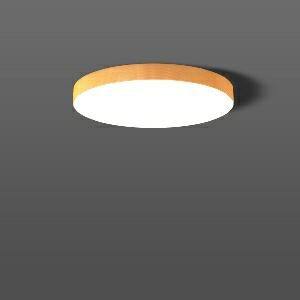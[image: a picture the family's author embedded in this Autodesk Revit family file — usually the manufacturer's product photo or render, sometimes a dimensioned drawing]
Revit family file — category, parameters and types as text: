
# Revit family: flatliner_slim_312283_002_1_33f7
name_source: partatom
category: Lighting Fixtures
units: mm (PartAtom-declared; Revit-internal decimal feet)

## family parameters
Cut with Voids When Loaded = No
Host = Face
Light Source = No
Part Type = Normal
Room Calculation Point = No
Round Connector Dimension = Use Diameter
Shared = No

## types (1)
- 982557.002 (1 x LED Modul 840, 2050 lm, 4000)
    Apparent Load = 27 VA
    CIE Flux Codes = 45 76 94 95 100
    Color Rendering = 80
    Color Temperature = 4000
    Default Elevation = 1800 mm
    Description = Series: FLATLINER SLIM
Decorative ceiling luminaire for interior decoration. Base luminaire prepared for the installation of fabric lampshade. Base: metal, white, powder-coated. Modular design: with the basic luminaire, a cylindrical fabric lampshade with a polycarbonate satin-finish diffuser must always be ordered separately. Fabric lampshade and diffuser can be assembled without the use of tools. 
Colour: white
Diameter: 418 mm
Height: 34 mm
Lamp: LED exchangeable
Socket: without socket
Colour temperature: 4000K
Colour rendering index (CRI): 80
System power: 24 W
Rated luminous flux: 2050 lm
Beam angle Down: 117°
Luminous efficiency: 85 lm/W
Control gear: AC Strom, dim.Ph.an-/abschnitt
Protection class: I
Type of protection: IP 20
    Height = 34 mm
    Lamp = 1 x LED Modul 840
    Lamp Light Flux = 2050 lm
    Lamp count = 1
    Length = 418 mm
    Lifetime = 50000 h
    Luminous efficacy = 76 lm/W
    Manufacturer = RZB
    ModVariant = No
    Model = 312283.002.1
    Mounting Place = Ceiling
    Mounting Type = Surface mounted
    Number of Poles = 1
    OnlyDefault = Yes
    Power Factor = 1
    Product Name = FLATLINER SLIM
    Product group = Surface mounted ceiling Fabric lampshade luminaires
    ProductGroupID = 313
    Protection Class = Protection class I
    Protection Degree = IP 20
    RLX_Detail_Level = 1
    RLX_Emergency_Light_Flux = 0 lm
    RLX_Emergency_Type = 0
    RLX_Emergency_Type_DB = No
    RlxData = <blob elided: 25221 chars, md5=c085847d>
    Socket = socket
    Standby Power = 0 W
    System Light Flux = 2050 lm
    System Power = 27 W
    Type Image = 312287.002_982442.0063_982444.002.jpg
    URL = http://relux.com
    VarID = 982557_002_b87f
    Voltage = 230 V
    Voltage Range = 220-240 V
    Weight = 0.00 kg
    Width = 0 mm  [stored 0 ft]

note: [stored X ft] marks values corroborated as IEEE doubles in the binary element streams (Revit-internal decimal feet)

## geometry (parser evidence)
native form markers: Blend x4, Sweep x12
no freeform markers — native parametric forms only
